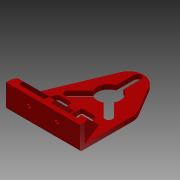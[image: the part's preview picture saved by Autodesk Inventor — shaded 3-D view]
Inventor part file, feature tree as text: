
AUTODESK INVENTOR PART (.ipt)
format: ipt  version: 2013 (Build 170138000, 138)  size: 358,912 bytes
history: native  units: mm
features: sketch x10, extrude x9, fillet x6, chamfer x3, hole x1
ambient origin geometry x8: Origin, YZ Plane, XZ Plane, XY Plane, X Axis, Y Axis, Z Axis, Center Point
feature tree (29):
  extrude  "Extrusion1"  Depth=4.0mm
  sketch  "Sketch4"  dims[d5=4.0mm d6=4.0mm]
  extrude  "Extrusion6"  Depth=4.0mm
  extrude  "Extrusion8"  Depth=12.0mm
  extrude  "Extrusion9"  Depth=5.0mm
  chamfer  "Chamfer4"  Distance=5.0mm
  chamfer  "Chamfer5"  Distance=5.0mm
  chamfer  "Chamfer6"  Distance=25.0mm
  fillet  "Fillet8"  Radius=11.84mm
  fillet  "Fillet9"  Radius=11.84mm
  fillet  "Fillet10"  Radius=5.0mm
  extrude  "Extrusion10"  Depth=5.0mm
  extrude  "Extrusion11"  Depth=5.0mm TaperAngle=0.0deg
  extrude  "Extrusion12"  Depth=25.0mm
  extrude  "Extrusion13"  Depth=0.142304mm
  extrude  "Extrusion14"  Depth=0.142304mm
  fillet  "Fillet11"  Radius=20.0mm
  fillet  "Fillet12"  Radius=20.0mm
  fillet  "Fillet13"  Radius=20.0mm
  hole  "Hole2"  [1 undecoded]
  sketch  "Sketch1"  dims[d3=40.0mm d4=4.0mm]
  sketch  "Sketch10"  dims[d7=12.0mm d8=12.0mm]
  sketch  "Sketch11"  dims[d9=16.5mm d10=5.0mm]
  sketch  "Sketch12"  dims[d13=10.0mm]
  sketch  "Sketch13"  dims[d14=3.0mm d38=5.0mm d39=0.0mm]
  sketch  "Sketch14"  dims[d87=25.0mm d88=5.0mm d89=0.0mm]
  sketch  "Sketch15"  dims[d94=25.0mm]
  sketch  "Sketch16"  dims[d96=25.0mm]
  sketch  "Sketch17"  dims[d97=25.0mm d98=25.0mm d99=11.84mm d100=11.84mm d101=5.0mm d102=5.0mm d103=5.0mm d104=0.0mm d105=25.0mm d107=0.142304mm d108=0.142304mm d109=20.0mm d110=0.0mm d111=20.0mm d112=20.0mm d113=45.0deg d114=20.0mm d115=20.0mm d116=45.0deg d117=20.0mm d118=20.0mm d119=45.0deg d120=2.0mm d121=2.0mm d122=2.0mm d123=5.0mm d124=0.0mm d125=5.0mm d126=0.0mm d127=25.0mm d129=5.0mm d130=0.0mm d131=100.0mm d146=8.0mm d147=8.0mm d148=8.0mm d152=5.0mm d153=0.0mm d154=8.0mm d155=8.0mm d156=5.0mm d157=0.0mm d158=16.0mm d159=16.0mm d160=2.0mm d161=10.0mm d162=10.0mm d163=25.0mm d164=25.0mm d165=4.0mm d166=6.0mm d167=4.0mm d168=2.0mm d169=90.0deg d170=8.0mm d171=20.594885mm]
note: 1 required parameter value undecoded (feature->parameter linkage not recoverable at this tier; creation-order binding heuristic only, values carry confidence <= 0.55)
